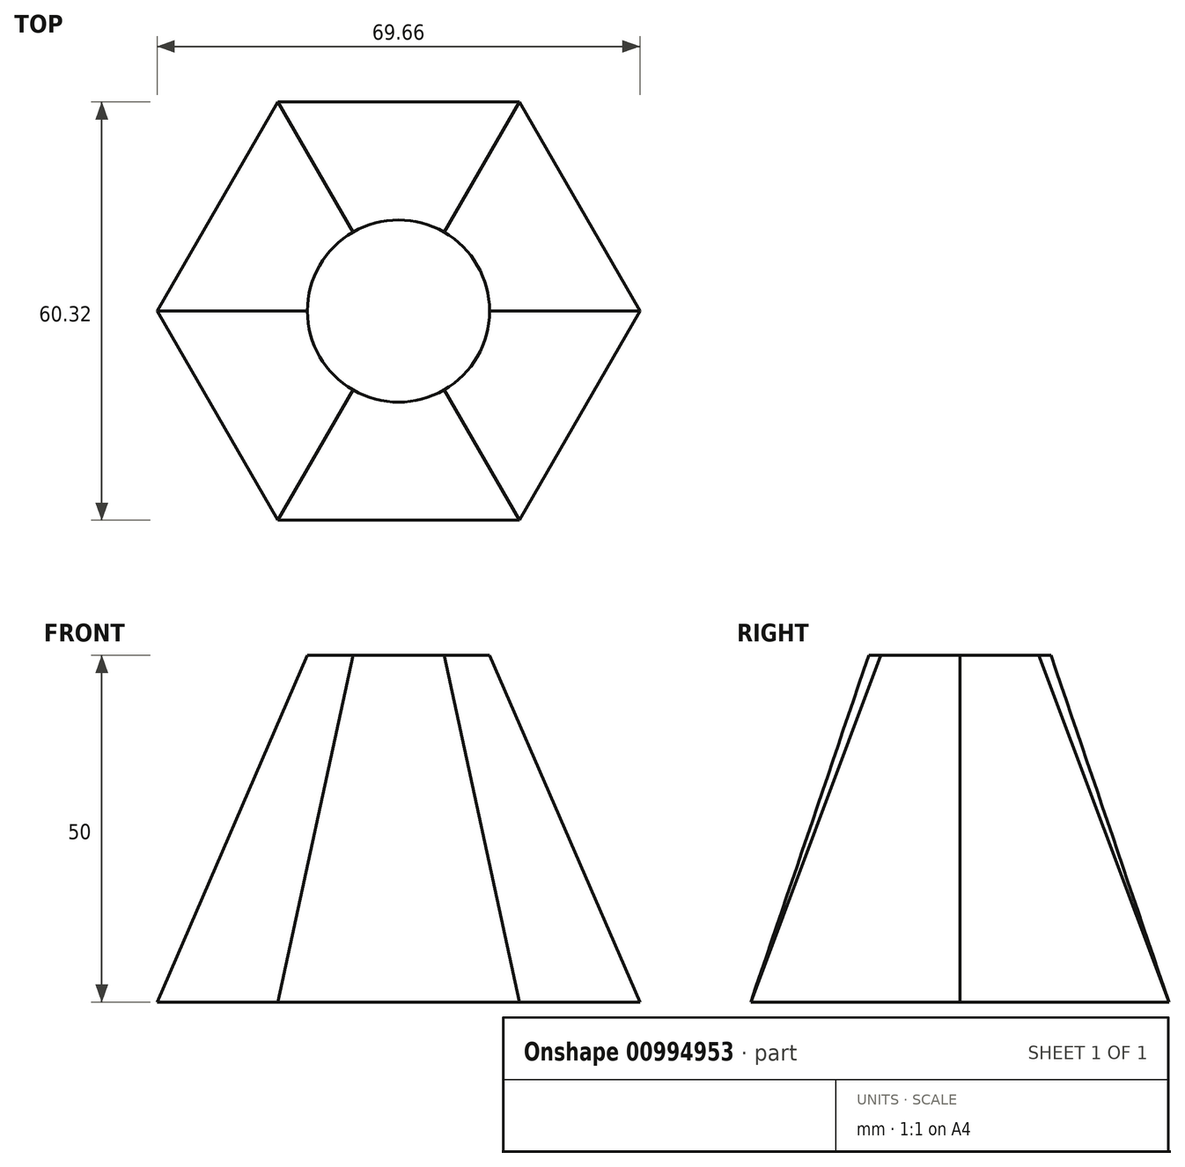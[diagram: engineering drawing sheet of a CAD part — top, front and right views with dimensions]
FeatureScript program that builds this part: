
annotation { "Feature Type Name" : "Feature", "Feature Type Description" : "" }
export const myFeature = defineFeature(function(context is Context, id is Id, definition is map)
    precondition{}
    {
        {
            var Q0;
            Q0=qCreatedBy(makeId("Top.planeOp"),FACE);
            var sketch = newSketch(context, id + "F0", { "sketchPlane" : qUnion([Q0])});
            skCircle(sketch, "E0.cCircle", {"center": v(0, 0) * mm, "radius": 30.16 * mm, "construction": true});
            skLineSegment(sketch, "E0.0", {"start": v(17.41, -30.16) * mm, "end": v(-17.41, -30.16) * mm});
            skLineSegment(sketch, "E0.1", {"start": v(-17.41, -30.16) * mm, "end": v(-34.83, 0) * mm});
            skLineSegment(sketch, "E0.2", {"start": v(-34.83, 0) * mm, "end": v(-17.41, 30.16) * mm});
            skLineSegment(sketch, "E0.3", {"start": v(-17.41, 30.16) * mm, "end": v(17.41, 30.16) * mm});
            skLineSegment(sketch, "E0.4", {"start": v(17.41, 30.16) * mm, "end": v(34.83, 0) * mm});
            skLineSegment(sketch, "E0.5", {"start": v(34.83, 0) * mm, "end": v(17.41, -30.16) * mm});
            skPoint(sketch, "E0.0.midPoint", {"position": v(0, -30.16) * mm});
            skSolve(sketch);
        }
        {
            var Q0;
            Q0=qCreatedBy(makeId("Top.planeOp"),FACE);
            cPlane(context, id + "F1", {"entities" : qUnion([Q0]), "cplaneType" : CPlaneType.OFFSET, "offset" : 50 * mm, "width" : 150 * mm, "height" : 150 * mm});
        }
        {
            var Q0;
            Q0=qCreatedBy(id+"F1.planeOp",FACE);
            var sketch = newSketch(context, id + "F2", { "sketchPlane" : qUnion([Q0])});
            skCircle(sketch, "E1", {"center": v(0, 0) * mm, "radius": 13.14 * mm});
            skSolve(sketch);
        }
        {
            var Q0;
            Q0=makeQuery(id+"F0.imprint","IMPRINT",FACE,{"disambiguationData":[TD([[makeQuery(id+"F0.imprint","IMPRINT",EDGE,{"derivedFrom":sQuery(id+"F0.wireOp",EDGE,"E0.0")}),-1.0]])]});
            var Q1;
            Q1=makeQuery(id+"F2.imprint","IMPRINT",FACE,{"disambiguationData":[TD([[makeQuery(id+"F2.imprint","IMPRINT",EDGE,{"derivedFrom":sQuery(id+"F2.wireOp",EDGE,"E1")}),1.0]])]});
            loft(context, id + "F3", {"sheetProfilesArray" : [{ "sheetProfileEntities" : qUnion([Q0]) }, { "sheetProfileEntities" : qUnion([Q1]) }]});
        }
    });
